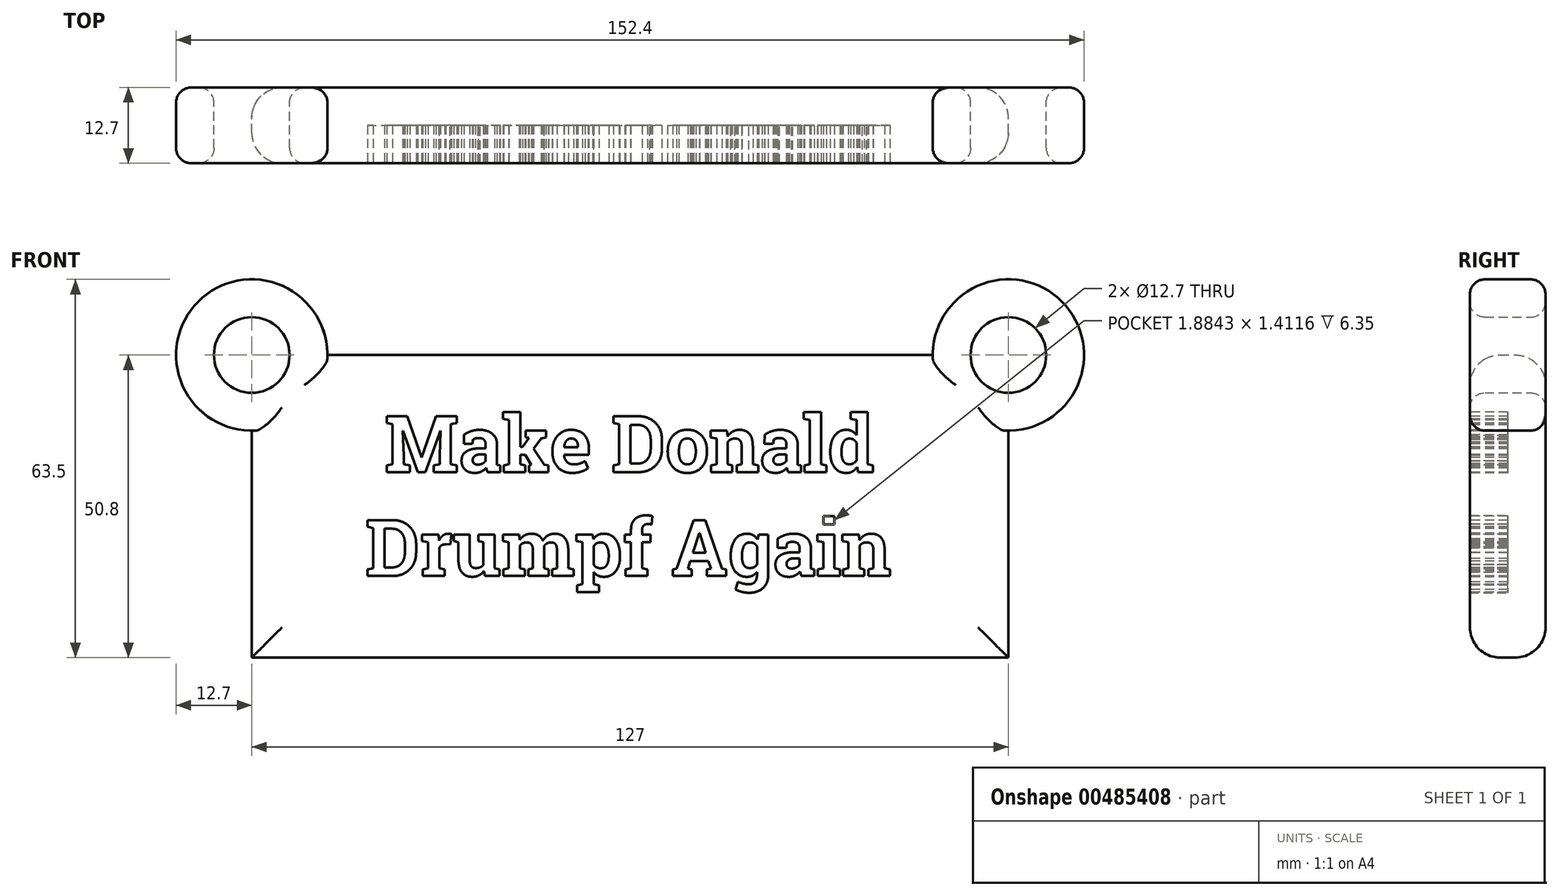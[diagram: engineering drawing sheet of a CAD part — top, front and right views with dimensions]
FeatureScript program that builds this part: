
annotation { "Feature Type Name" : "Feature", "Feature Type Description" : "" }
export const myFeature = defineFeature(function(context is Context, id is Id, definition is map)
    precondition{}
    {
        {
            var Q0;
            Q0=qCreatedBy(makeId("Front.planeOp"),FACE);
            var sketch = newSketch(context, id + "F0", { "sketchPlane" : qUnion([Q0])});
            skLineSegment(sketch, "E0.bottom", {"start": v(-127, 50.8) * mm, "end": v(0, 50.8) * mm});
            skLineSegment(sketch, "E0.top", {"start": v(-127, 0) * mm, "end": v(0, 0) * mm});
            skLineSegment(sketch, "E0.left", {"start": v(-127, 50.8) * mm, "end": v(-127, 0) * mm});
            skLineSegment(sketch, "E0.right", {"start": v(0, 50.8) * mm, "end": v(0, 0) * mm});
            skCircle(sketch, "E1", {"center": v(-127, 50.8) * mm, "radius": 6.35 * mm});
            skCircle(sketch, "E2", {"center": v(0, 50.8) * mm, "radius": 12.7 * mm});
            skCircle(sketch, "E3", {"center": v(0, 50.8) * mm, "radius": 6.35 * mm});
            skCircle(sketch, "E4", {"center": v(-127, 50.8) * mm, "radius": 12.7 * mm});
            skSolve(sketch);
        }
        {
            var Q0;
            Q0=qSketchRegion(id+"F0",true);
            extrude(context, id + "F1", {"entities" : qUnion([Q0]), "depth" : 12.7 * mm});
        }
        {
            var Q0;
            Q0=makeQuery(id+"F1.opExtrude","CAP_FACE",FACE,{"disambiguationData":[OSD([sQuery(id+"F0.wireOp",EDGE,"E0.bottom"),sQuery(id+"F0.wireOp",EDGE,"E0.top"),sQuery(id+"F0.wireOp",EDGE,"E0.left"),sQuery(id+"F0.wireOp",EDGE,"E0.right"),sQuery(id+"F0.wireOp",EDGE,"E1"),sQuery(id+"F0.wireOp",EDGE,"E2"),sQuery(id+"F0.wireOp",EDGE,"E3"),sQuery(id+"F0.wireOp",EDGE,"E4")])],"isStart":false});
            var sketch = newSketch(context, id + "F2", { "sketchPlane" : qUnion([Q0])});
            skText(sketch, "E5", { "text": " Make Donald\nDrumpf Again", "fontName": "RobotoSlab-Bold.ttf"});
            const initialGuessF2  = {"E5": [-0.10795, 0.03113, 1, 0, 0.00951]};
            skSetInitialGuess(sketch, initialGuessF2);
            skSolve(sketch);
        }
        {
            var Q0;
            Q0=qSketchRegion(id+"F2",true);
            extrude(context, id + "F3", {"entities" : qUnion([Q0]), "operationType" : NewBodyOperationType.REMOVE, "oppositeDirection" : true, "depth" : 6.35 * mm});
        }
        {
            var Q0;
            Q0=makeQuery(id+"F1.opExtrude","CAP_EDGE",EDGE,{"disambiguationData":[OSD([sQuery(id+"F0.wireOp",EDGE,"E1")])],"isStart":false});
            var Q1;
            Q1=makeQuery(id+"F1.opExtrude","CAP_EDGE",EDGE,{"disambiguationData":[OSD([sQuery(id+"F0.wireOp",EDGE,"E3")])],"isStart":false});
            var Q2;
            Q2=makeQuery(id+"F1.opExtrude","CAP_EDGE",EDGE,{"disambiguationData":[OSD([sQuery(id+"F0.wireOp",EDGE,"E1")])],"isStart":true});
            var Q3;
            Q3=makeQuery(id+"F1.opExtrude","CAP_EDGE",EDGE,{"disambiguationData":[OSD([sQuery(id+"F0.wireOp",EDGE,"E3")])],"isStart":true});
            var Q4;
            Q4=makeQuery(id+"F1.opExtrude","CAP_EDGE",EDGE,{"disambiguationData":[OSD([sQuery(id+"F0.wireOp",EDGE,"E4")])],"isStart":false});
            var Q5;
            Q5=makeQuery(id+"F1.opExtrude","CAP_EDGE",EDGE,{"disambiguationData":[OSD([sQuery(id+"F0.wireOp",EDGE,"E4")])],"isStart":true});
            var Q6;
            Q6=makeQuery(id+"F1.opExtrude","CAP_EDGE",EDGE,{"disambiguationData":[OSD([sQuery(id+"F0.wireOp",EDGE,"E2")])],"isStart":true});
            var Q7;
            Q7=makeQuery(id+"F1.opExtrude","CAP_EDGE",EDGE,{"disambiguationData":[OSD([sQuery(id+"F0.wireOp",EDGE,"E2")])],"isStart":false});
            fillet(context, id + "F4", {"entities" : qUnion([Q0, Q1, Q2, Q3, Q4, Q5, Q6, Q7]), "radius" : 2.54 * mm, "tangentPropagation" : true, "allowEdgeOverflow" : false});
        }
        {
            var Q0;
            Q0=makeQuery(id+"F1.opExtrude","CAP_EDGE",EDGE,{"disambiguationData":[OSD([sQuery(id+"F0.wireOp",EDGE,"E0.bottom")])],"isStart":false});
            var Q1;
            Q1=makeQuery(id+"F1.opExtrude","CAP_EDGE",EDGE,{"disambiguationData":[OSD([sQuery(id+"F0.wireOp",EDGE,"E0.bottom")])],"isStart":true});
            var Q2;
            Q2=makeQuery(id+"F1.opExtrude","CAP_EDGE",EDGE,{"disambiguationData":[OSD([sQuery(id+"F0.wireOp",EDGE,"E0.right")])],"isStart":false});
            var Q3;
            Q3=makeQuery(id+"F1.opExtrude","CAP_EDGE",EDGE,{"disambiguationData":[OSD([sQuery(id+"F0.wireOp",EDGE,"E0.right")])],"isStart":true});
            var Q4;
            Q4=makeQuery(id+"F1.opExtrude","CAP_EDGE",EDGE,{"disambiguationData":[OSD([sQuery(id+"F0.wireOp",EDGE,"E0.top")])],"isStart":false});
            var Q5;
            Q5=makeQuery(id+"F1.opExtrude","CAP_EDGE",EDGE,{"disambiguationData":[OSD([sQuery(id+"F0.wireOp",EDGE,"E0.left")])],"isStart":false});
            var Q6;
            Q6=makeQuery(id+"F1.opExtrude","CAP_EDGE",EDGE,{"disambiguationData":[OSD([sQuery(id+"F0.wireOp",EDGE,"E0.top")])],"isStart":true});
            var Q7;
            Q7=makeQuery(id+"F1.opExtrude","CAP_EDGE",EDGE,{"disambiguationData":[OSD([sQuery(id+"F0.wireOp",EDGE,"E0.left")])],"isStart":true});
            fillet(context, id + "F5", {"entities" : qUnion([Q0, Q1, Q2, Q3, Q4, Q5, Q6, Q7]), "radius" : 5.08 * mm, "tangentPropagation" : true, "allowEdgeOverflow" : false});
        }
    });
